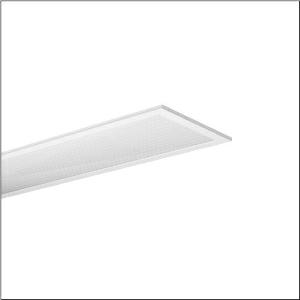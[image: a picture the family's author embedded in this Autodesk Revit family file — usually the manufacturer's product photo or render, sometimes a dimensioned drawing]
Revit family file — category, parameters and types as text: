
# Revit family: apollon_r__21_linear_51mq14wd2t12_0b39
name_source: partatom
category: Lighting Fixtures
units: mm (PartAtom-declared; Revit-internal decimal feet)

## family parameters
Cut with Voids When Loaded = No
Host = Face
Light Source = No
Part Type = Normal
Room Calculation Point = No
Round Connector Dimension = Use Diameter
Shared = No

## types (1)
- --- (1 x LED 2700 K ... 6500 K, 4200 lm, 44 W, 6500K)
    Apparent Load = 44 VA
    CIE Flux Codes = 60 87 97 100 100
    Color Rendering = 80
    Color Temperature = 6500K
    Default Elevation = 1800 mm
    Description = Apollon® 21 linear, office luminaire, primary optical cover: micro prismatic cover, of PMMA, CAT 2 (L<= 3000cd/m²), light emission: direct distribution, primary light characteristic: symmetric, installation type: lay-in mounting, LED, rated luminous flux: 4.200lm, luminous efficacy: 96lm/W, light colour: 8tw, colour temperature: 2700..6500K, with terminal, 5-pole, mains connection: 220..240V, AC, 50/60Hz, rated input power: 44W, housing, of aluminium, coated, pure white, length: 1.245mm, width: 307mm, height: 30mm, housing upper side, of sheet steel, galvanised, protection rating (complete): IP20, protection rating (lamp compartment, on room side): IP50, insulation class (complete): insulation class I (protective earthing), certification: CE, ENEC, packaging unit: 1 piece
    Height = 0 mm  [stored 0 ft]
    Lamp = 1 x LED 2700 K ... 6500 K
    Lamp Light Flux = 4200 lm
    Lamp Power = 44 W
    Lamp count = 1
    Length = 1245 mm
    Luminous efficacy = 95 lm/W
    Manufacturer = Siteco
    ModVariant = No
    Model = 51MQ14WD2T12
    Mounting Place = Ceiling
    Mounting Type = Recessed
    Number of Poles = 1
    OnlyDefault = Yes
    Power Factor = 1
    Product Name = Apollon® 21 linear
    Product group = office luminaire | ceiling recessed
    ProductGroupID = 401
    Protection Class = Protection class I
    Protection Degree = IP 20
    RLX_Detail_Level = 1
    RLX_Emergency_Light_Flux = 0 lm
    RLX_Emergency_Type = 0
    RLX_Emergency_Type_DB = No
    RlxData = <blob elided: 17565 chars, md5=11408e82>
    Socket = socket
    Standby Power = 0 W
    System Light Flux = 4200 lm
    System Power = 44 W
    Type Comments = individual setting: CCT=6500K, colour temperature 6500K
    Type Image = l_1291045.jpg
    URL = http://relux.com
    VarID = @adj_152827
    Voltage = 0 V
    Weight = 0.00 kg
    Width = 307 mm

note: [stored X ft] marks values corroborated as IEEE doubles in the binary element streams (Revit-internal decimal feet)

## geometry (parser evidence)
native form markers: Blend x4, Sweep x12
no freeform markers — native parametric forms only
